# Revit family: Shower-Valve_Trim-KOHLER-Taut-K-24572X_1
name_source: partatom
category: Specialty Equipment
units: mm (PartAtom-declared; Revit-internal decimal feet)

## family parameters
Cut with Voids When Loaded = No
Host = Face
OmniClass Number = 23.31.25.00
OmniClass Title = Toilet and Bath Specialties
Part Type = Normal
Room Calculation Point = No
Round Connector Dimension = Use Diameter
Shared = No

## types (1)
- CP-Polished Chrome
    ADA Compliant = No
    Assembly Code = C1030200
    Date Modified = 03/08/2023
    Default Elevation = 42"
    Description = Pin Recessed Bath Shower Valve Mixer
    Finish = Kohler-Metal-CP-Polished_Chrome
    Handle Clearance = 3 7/16"
    Height = 5 3/4"
    Length = 2 13/16"
    Manufacturer = Kohler Co.
    Master Format 2014 = 10 28 00
    Master Format 2014 Name = Toilet, Bath, and Laundry Accessories
    Material = Premium Metal Construction
    Model = K-24572X-4A-CP
    Product Name = Taut
    Type = 1
    URL = https://www.kohler.co.th
    WaterSense Certified = No
    Width = 4 5/16"

## geometry (parser evidence)
native form markers: Sweep x9
no freeform markers — native parametric forms only
